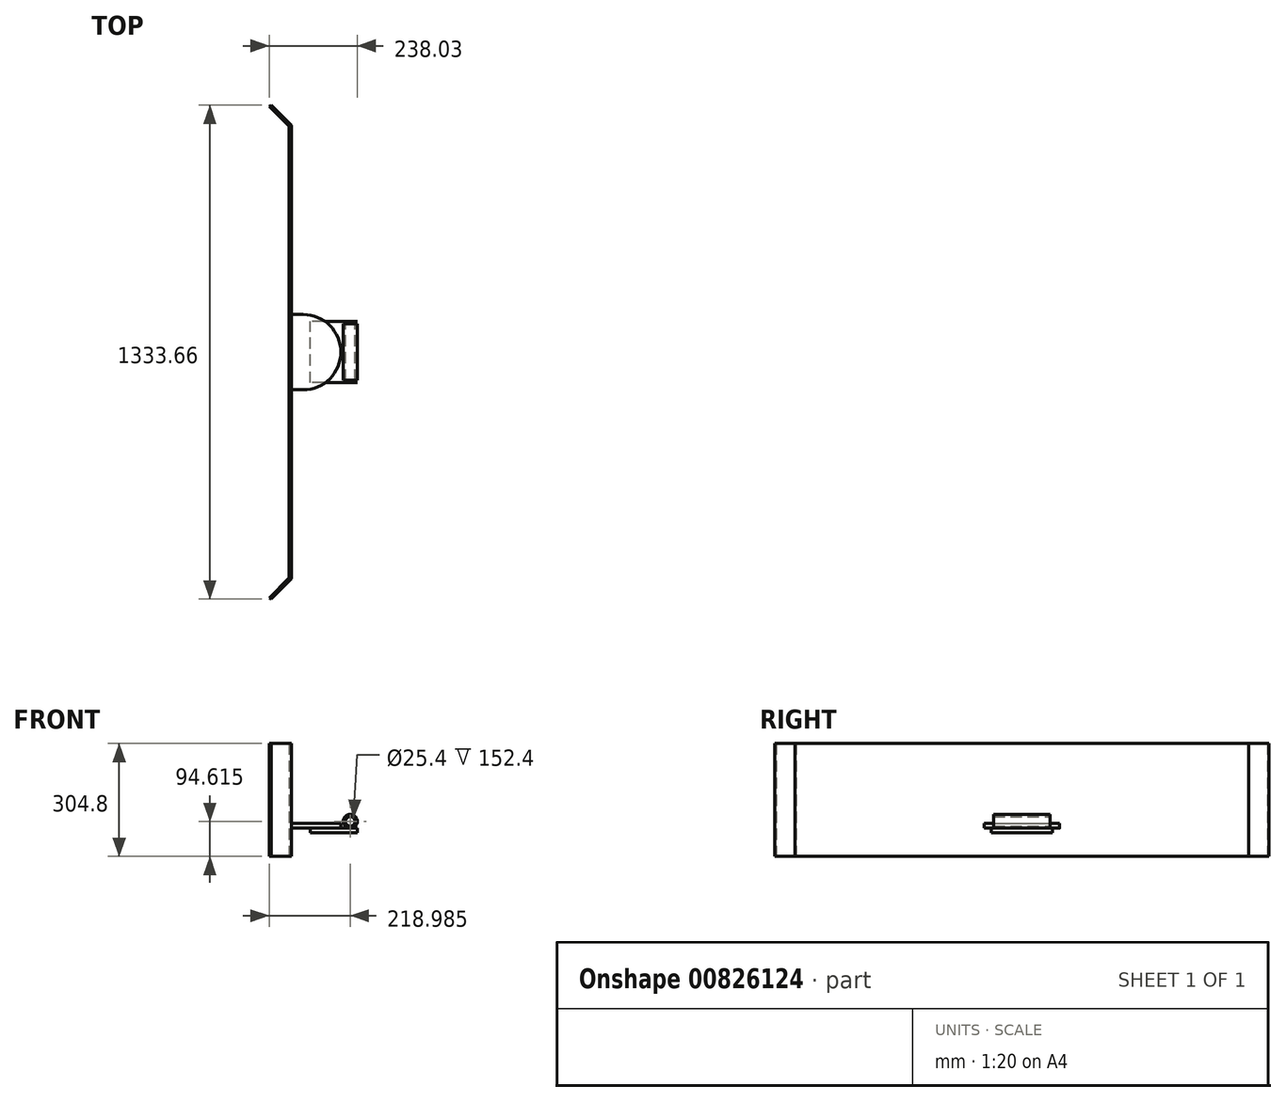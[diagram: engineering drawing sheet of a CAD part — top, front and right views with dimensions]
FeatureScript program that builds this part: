
annotation { "Feature Type Name" : "Feature", "Feature Type Description" : "" }
export const myFeature = defineFeature(function(context is Context, id is Id, definition is map)
    precondition{}
    {
        {
            var Q0;
            Q0=qCreatedBy(makeId("Top.planeOp"),FACE);
            var sketch = newSketch(context, id + "F0", { "sketchPlane" : qUnion([Q0])});
            skLineSegment(sketch, "E0", {"start": v(0, 379.64) * mm, "end": v(0, -412.48) * mm, "construction": true});
            skLineSegment(sketch, "E1", {"start": v(123.75, -609.6) * mm, "end": v(123.75, 609.6) * mm});
            skLineSegment(sketch, "E2", {"start": v(123.75, 609.6) * mm, "end": v(69.87, 663.48) * mm});
            skLineSegment(sketch, "E3", {"start": v(123.75, -609.6) * mm, "end": v(69.87, -663.48) * mm});
            skLineSegment(sketch, "E4", {"start": v(0, 0) * mm, "end": v(366.21, 0) * mm, "construction": true});
            skLineSegment(sketch, "E5.0", {"start": v(130.1, -612.23) * mm, "end": v(130.1, 612.23) * mm});
            skLineSegment(sketch, "E6.0", {"start": v(130.1, -612.23) * mm, "end": v(75.57, -666.77) * mm});
            skLineSegment(sketch, "E7.0", {"start": v(130.1, 612.23) * mm, "end": v(75.44, 666.9) * mm});
            skLineSegment(sketch, "E8", {"start": v(69.87, -663.48) * mm, "end": v(75.57, -666.77) * mm});
            skLineSegment(sketch, "E9", {"start": v(69.87, 663.48) * mm, "end": v(75.44, 666.9) * mm});
            skSolve(sketch);
        }
        {
            var Q0;
            Q0=makeQuery(id+"F0.imprint","IMPRINT",FACE,{"disambiguationData":[TD([[makeQuery(id+"F0.imprint","IMPRINT",EDGE,{"derivedFrom":sQuery(id+"F0.wireOp",EDGE,"E1")}),-1.0]])]});
            extrude(context, id + "F1", {"entities" : qUnion([Q0]), "depth" : 304.8 * mm, "offsetDistance" : 25.4 * mm});
        }
        {
            var Q0;
            Q0=qCreatedBy(makeId("Top.planeOp"),FACE);
            cPlane(context, id + "F2", {"entities" : qUnion([Q0]), "cplaneType" : CPlaneType.OFFSET, "offset" : 76.2 * mm, "width" : 152.4 * mm, "height" : 152.4 * mm});
        }
        {
            var Q0;
            Q0=qCreatedBy(id+"F2.planeOp",FACE);
            var sketch = newSketch(context, id + "F3", { "sketchPlane" : qUnion([Q0])});
            skLineSegment(sketch, "E10.0.0", {"start": v(130.1, -612.23) * mm, "end": v(130.1, 612.23) * mm});
            skLineSegment(sketch, "E10.0.2", {"start": v(130.1, 612.23) * mm, "end": v(130.1, 203.2) * mm});
            skLineSegment(sketch, "E11", {"start": v(0, 0) * mm, "end": v(323.7, 0) * mm, "construction": true});
            skArc(sketch, "E12", {"start": v(161.85, -101.6) * mm, "mid": v(263.45, 0) * mm, "end": v(161.85, 101.6) * mm});
            skPoint(sketch, "E13.end.orphan", {"position": v(240.7, 50.94) * mm});
            skPoint(sketch, "E14.orphan", {"position": v(240.7, -50.94) * mm});
            skLineSegment(sketch, "E15", {"start": v(161.85, 101.6) * mm, "end": v(130.1, 101.6) * mm});
            skLineSegment(sketch, "E16.MirrorCS", {"start": v(0, 203.2) * mm, "end": v(323.7, 203.2) * mm, "construction": true});
            skLineSegment(sketch, "E17.MirrorCS", {"start": v(161.85, -101.6) * mm, "end": v(130.1, -101.6) * mm});
            skPoint(sketch, "E18.orphan", {"position": v(130.1, -612.23) * mm});
            skLineSegment(sketch, "E19.trimOffspring", {"start": v(130.1, 101.6) * mm, "end": v(130.1, -101.6) * mm});
            skSolve(sketch);
        }
        {
            var Q0;
            Q0=makeQuery(id+"F3.imprint","IMPRINT",FACE,{"disambiguationData":[TD([[makeQuery(id+"F3.imprint","IMPRINT",EDGE,{"derivedFrom":sQuery(id+"F3.wireOp",EDGE,"E12")}),1.0]])]});
            extrude(context, id + "F4", {"entities" : qUnion([Q0]), "operationType" : NewBodyOperationType.ADD, "depth" : 12.7 * mm, "offsetDistance" : 25.4 * mm});
        }
        {
            var Q0;
            Q0=makeQuery(id+"F4.opExtrude","CAP_FACE",FACE,{"disambiguationData":[OSD([sQuery(id+"F3.wireOp",EDGE,"E12"),sQuery(id+"F3.wireOp",EDGE,"E15"),sQuery(id+"F3.wireOp",EDGE,"E17.MirrorCS"),sQuery(id+"F3.wireOp",EDGE,"E19.trimOffspring")])],"isStart":true});
            var sketch = newSketch(context, id + "F5", { "sketchPlane" : qUnion([Q0])});
            skLineSegment(sketch, "E20.bottom", {"start": v(307.9, 82.55) * mm, "end": v(180.9, 82.55) * mm});
            skLineSegment(sketch, "E20.top", {"start": v(307.9, -82.55) * mm, "end": v(180.9, -82.55) * mm});
            skLineSegment(sketch, "E20.left", {"start": v(307.9, 82.55) * mm, "end": v(307.9, -82.55) * mm});
            skLineSegment(sketch, "E20.right", {"start": v(180.9, 82.55) * mm, "end": v(180.9, -82.55) * mm});
            skPoint(sketch, "E20.middle", {"position": v(244.4, 0) * mm});
            skSolve(sketch);
        }
        {
            var Q0;
            Q0 = qSketchRegion(id + "F5", true);
            extrude(context, id + "F6", {"entities" : qUnion([Q0]), "operationType" : NewBodyOperationType.ADD, "depth" : 12.7 * mm, "offsetDistance" : 25.4 * mm});
        }
        {
            var Q0;
            Q0=qCreatedBy(makeId("Front.planeOp"),FACE);
            var sketch = newSketch(context, id + "F7", { "sketchPlane" : qUnion([Q0])});
            skCircle(sketch, "E21", {"center": v(288.85, 94.62) * mm, "radius": 19.05 * mm});
            skCircle(sketch, "E22", {"center": v(288.85, 94.62) * mm, "radius": 12.7 * mm});
            skSolve(sketch);
        }
        {
            var Q0;
            Q0=makeQuery(id+"F7.imprint","IMPRINT",FACE,{"disambiguationData":[TD([[makeQuery(id+"F7.imprint","IMPRINT",EDGE,{"derivedFrom":sQuery(id+"F7.wireOp",EDGE,"E21")}),1.0]])]});
            extrude(context, id + "F8", {"entities" : qUnion([Q0]), "endBound" : BoundingType.SYMMETRIC, "depth" : 152.4 * mm, "offsetDistance" : 25.4 * mm});
        }
    });
